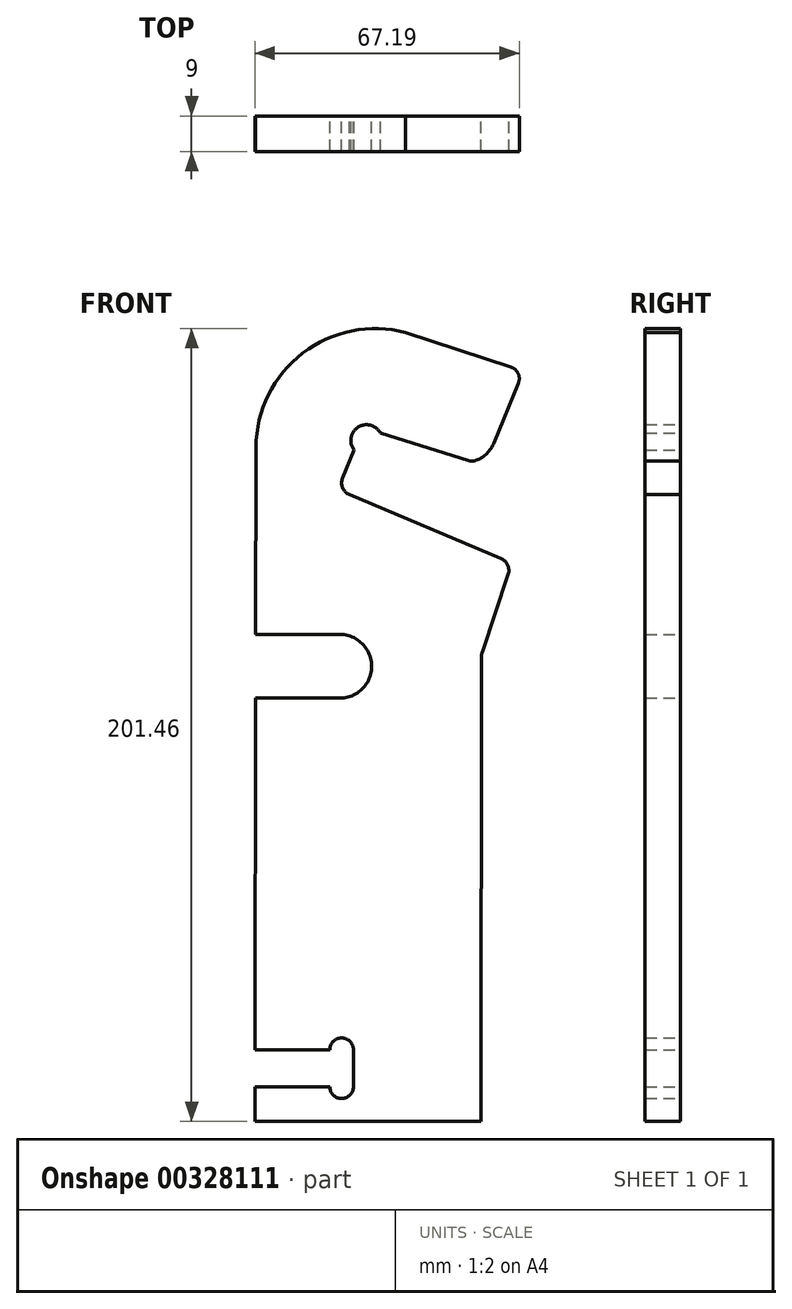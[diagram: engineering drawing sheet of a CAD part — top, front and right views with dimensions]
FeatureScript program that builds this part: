
annotation { "Feature Type Name" : "Feature", "Feature Type Description" : "" }
export const myFeature = defineFeature(function(context is Context, id is Id, definition is map)
    precondition{}
    {
        {
            var Q0;
            Q0=qCreatedBy(makeId("Front.planeOp"),FACE);
            var sketch = newSketch(context, id + "F0", { "sketchPlane" : qUnion([Q0])});
            skArc(sketch, "E0", {"start": v(12.26, 34.16) * mm, "mid": v(20.35, 26.05) * mm, "end": v(12.24, 17.96) * mm});
            skLineSegment(sketch, "E1", {"start": v(12.24, 17.96) * mm, "end": v(-9.16, 17.99) * mm});
            skLineSegment(sketch, "E2", {"start": v(-9.16, 17.99) * mm, "end": v(-9.32, -89.52) * mm});
            skLineSegment(sketch, "E3", {"start": v(-9.32, -89.52) * mm, "end": v(48.13, -89.6) * mm});
            skLineSegment(sketch, "E4", {"start": v(48.13, -89.6) * mm, "end": v(48.3, 28.7) * mm});
            skArc(sketch, "E5", {"start": v(48.3, 28.7) * mm, "mid": v(48.34, 29.2) * mm, "end": v(48.46, 29.7) * mm});
            skLineSegment(sketch, "E6", {"start": v(48.46, 29.7) * mm, "end": v(55.05, 49.38) * mm});
            skArc(sketch, "E7", {"start": v(55.05, 49.38) * mm, "mid": v(54.93, 51.79) * mm, "end": v(53.2, 53.47) * mm});
            skLineSegment(sketch, "E8", {"start": v(53.2, 53.47) * mm, "end": v(14.74, 69.69) * mm});
            skArc(sketch, "E9", {"start": v(14.74, 69.69) * mm, "mid": v(13, 71.4) * mm, "end": v(12.98, 73.86) * mm});
            skLineSegment(sketch, "E10", {"start": v(12.98, 73.86) * mm, "end": v(15.89, 81.01) * mm});
            skArc(sketch, "E11", {"start": v(15.89, 81.01) * mm, "mid": v(16.94, 86.81) * mm, "end": v(22.63, 85.27) * mm});
            skLineSegment(sketch, "E12", {"start": v(22.63, 85.27) * mm, "end": v(45.01, 78.33) * mm});
            skArc(sketch, "E13", {"start": v(45.01, 78.33) * mm, "mid": v(46.01, 78.2) * mm, "end": v(47, 78.4) * mm});
            skArc(sketch, "E14", {"start": v(47, 78.4) * mm, "mid": v(49.69, 80.16) * mm, "end": v(51.47, 82.83) * mm});
            skLineSegment(sketch, "E15", {"start": v(51.47, 82.83) * mm, "end": v(57.65, 98.06) * mm});
            skArc(sketch, "E16", {"start": v(57.65, 98.06) * mm, "mid": v(57.6, 100.45) * mm, "end": v(55.81, 102.04) * mm});
            skLineSegment(sketch, "E17", {"start": v(55.81, 102.04) * mm, "end": v(29, 110.89) * mm});
            skArc(sketch, "E18", {"start": v(29, 110.89) * mm, "mid": v(2.86, 105.6) * mm, "end": v(-9.04, 81.71) * mm});
            skLineSegment(sketch, "E19", {"start": v(-9.04, 81.71) * mm, "end": v(-9.14, 34.19) * mm});
            skLineSegment(sketch, "E20", {"start": v(-9.14, 34.19) * mm, "end": v(12.26, 34.16) * mm});
            skLineSegment(sketch, "E21", {"start": v(-19.3, -76.73) * mm, "end": v(-19.3, -75.33) * mm});
            skArc(sketch, "E22", {"start": v(-19.3, -75.33) * mm, "mid": v(-18.12, -72.5) * mm, "end": v(-15.3, -71.33) * mm});
            skLineSegment(sketch, "E23", {"start": v(-15.3, -71.33) * mm, "end": v(9.74, -71.37) * mm});
            skArc(sketch, "E24", {"start": v(9.74, -71.37) * mm, "mid": v(12.75, -68.37) * mm, "end": v(15.74, -71.38) * mm});
            skLineSegment(sketch, "E25", {"start": v(15.74, -71.38) * mm, "end": v(15.73, -80.78) * mm});
            skArc(sketch, "E26", {"start": v(15.73, -80.78) * mm, "mid": v(12.72, -83.77) * mm, "end": v(9.73, -80.77) * mm});
            skLineSegment(sketch, "E27", {"start": v(9.73, -80.77) * mm, "end": v(-15.3, -80.73) * mm});
            skArc(sketch, "E28", {"start": v(-15.3, -80.73) * mm, "mid": v(-18.13, -79.56) * mm, "end": v(-19.3, -76.73) * mm});
            skLineSegment(sketch, "E29", {"start": v(39.17, -62.62) * mm, "end": v(30.17, -62.6) * mm});
            skArc(sketch, "E30", {"start": v(30.17, -62.6) * mm, "mid": v(27, -59.42) * mm, "end": v(30.18, -56.25) * mm});
            skLineSegment(sketch, "E31", {"start": v(30.18, -56.25) * mm, "end": v(30.3, 31.05) * mm});
            skArc(sketch, "E32", {"start": v(30.3, 31.05) * mm, "mid": v(27.13, 34.23) * mm, "end": v(30.31, 37.4) * mm});
            skLineSegment(sketch, "E33", {"start": v(30.31, 37.4) * mm, "end": v(39.31, 37.38) * mm});
            skArc(sketch, "E34", {"start": v(39.31, 37.38) * mm, "mid": v(42.48, 34.2) * mm, "end": v(39.3, 31.03) * mm});
            skLineSegment(sketch, "E35", {"start": v(39.3, 31.03) * mm, "end": v(39.18, -56.27) * mm});
            skArc(sketch, "E36", {"start": v(39.18, -56.27) * mm, "mid": v(42.35, -59.45) * mm, "end": v(39.17, -62.62) * mm});
            skSolve(sketch);
        }
        {
            var Q0;
            Q0=makeQuery(id+"F0.imprint","IMPRINT",FACE,{"disambiguationData":[TD([[makeQuery(id+"F0.imprint","IMPRINT",EDGE,{"derivedFrom":sQuery(id+"F0.wireOp",EDGE,"E29")}),-1.0]])]});
            var Q1;
            {var subQ0=sQuery(id+"F0.wireOp",EDGE,"E24");Q1=makeQuery(id+"F0.imprint","IMPRINT",FACE,{"disambiguationData":[TD([[makeQuery(id+"F0.imprint","IMPRINT",EDGE,{"derivedFrom":subQ0}),-1.0]])]});}
            var Q2;
            Q2=makeQuery(id+"F0.imprint","IMPRINT",FACE,{"disambiguationData":[TD([[makeQuery(id+"F0.imprint","IMPRINT",EDGE,{"derivedFrom":sQuery(id+"F0.wireOp",EDGE,"E0")}),1.0]])]});
            extrude(context, id + "F1", {"entities" : qUnion([Q0, Q1, Q2]), "depth" : 18 * mm});
        }
        {
            var Q0;
            {var subQ0=sQuery(id+"F0.wireOp",EDGE,"E24");Q0=makeQuery(id+"F0.imprint","IMPRINT",FACE,{"disambiguationData":[TD([[makeQuery(id+"F0.imprint","IMPRINT",EDGE,{"derivedFrom":subQ0}),-1.0]])]});}
            var Q1;
            Q1=makeQuery(id+"F0.imprint","IMPRINT",FACE,{"disambiguationData":[TD([[makeQuery(id+"F0.imprint","IMPRINT",EDGE,{"derivedFrom":sQuery(id+"F0.wireOp",EDGE,"E29")}),-1.0]])]});
            extrude(context, id + "F2", {"entities" : qUnion([Q0, Q1]), "operationType" : NewBodyOperationType.REMOVE, "depth" : 9 * mm});
        }
    });
